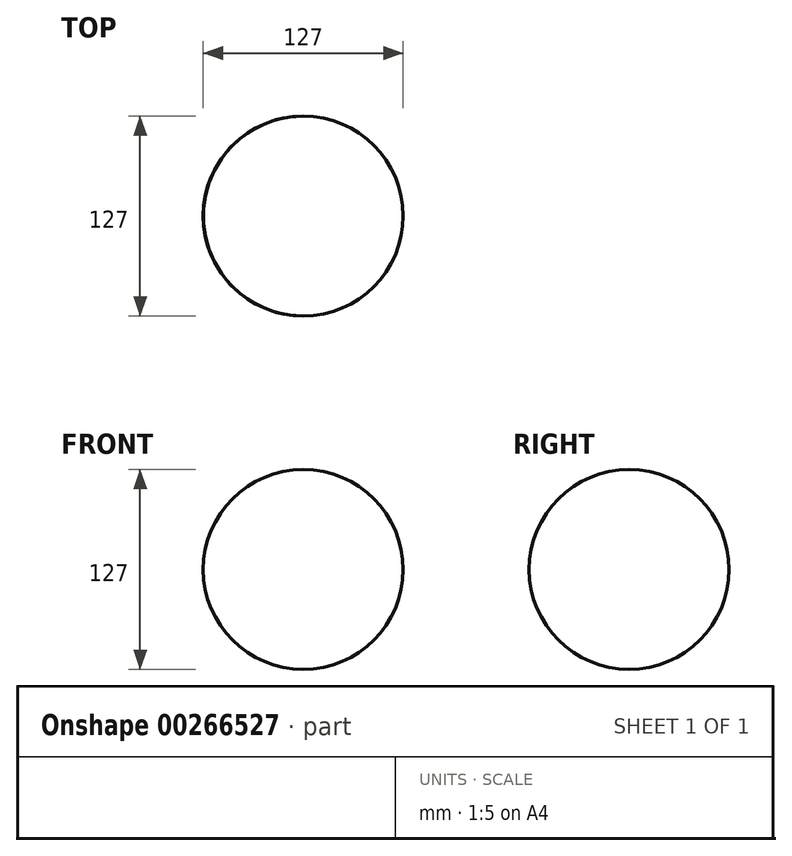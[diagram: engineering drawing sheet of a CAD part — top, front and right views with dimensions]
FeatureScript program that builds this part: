
annotation { "Feature Type Name" : "Feature", "Feature Type Description" : "" }
export const myFeature = defineFeature(function(context is Context, id is Id, definition is map)
    precondition{}
    {
        {
            var Q0;
            Q0=qCreatedBy(makeId("Top.planeOp"),FACE);
            var sketch = newSketch(context, id + "F0", { "sketchPlane" : qUnion([Q0])});
            skLineSegment(sketch, "E0.bottom", {"start": v(-63.5, 63.5) * mm, "end": v(0, 63.5) * mm});
            skLineSegment(sketch, "E0.top", {"start": v(-63.5, -63.5) * mm, "end": v(0, -63.5) * mm});
            skLineSegment(sketch, "E0.left", {"start": v(-63.5, 63.5) * mm, "end": v(-63.5, -63.5) * mm});
            skLineSegment(sketch, "E0.right", {"start": v(0, 63.5) * mm, "end": v(0, -63.5) * mm});
            skSolve(sketch);
        }
        {
            var Q0;
            Q0=makeQuery(id+"F0.imprint","IMPRINT",FACE,{"disambiguationData":[TD([[makeQuery(id+"F0.imprint","IMPRINT",EDGE,{"derivedFrom":sQuery(id+"F0.wireOp",EDGE,"E0.bottom")}),-1.0]])]});
            var Q1;
            Q1=sQuery(id+"F0.wireOp",EDGE,"E0.right");
            revolve(context, id + "F1", {"entities" : qUnion([Q0]), "axis" : qUnion([Q1]), "revolveType" : RevolveType.FULL});
        }
        {
            var Q0;
            Q0=qCreatedBy(makeId("Top.planeOp"),FACE);
            var sketch = newSketch(context, id + "F2", { "sketchPlane" : qUnion([Q0])});
            skArc(sketch, "E1", {"start": v(0, 63.5) * mm, "mid": v(63.5, 0) * mm, "end": v(0, -63.5) * mm});
            skLineSegment(sketch, "E2", {"start": v(0, -63.5) * mm, "end": v(0, 63.5) * mm});
            skSolve(sketch);
        }
        {
            var Q0;
            Q0 = qSketchRegion(id + "F2", true);
            var Q1;
            Q1=sQuery(id+"F2.wireOp",EDGE,"E1");
            var Q2;
            Q2=sQuery(id+"F2.wireOp",EDGE,"E2");
            var Q3;
            Q3=sQuery(id+"F2.wireOp",EDGE,"E2");
            revolve(context, id + "F3", {"operationType" : NewBodyOperationType.INTERSECT, "entities" : qUnion([Q0]), "surfaceEntities" : qUnion([Q1, Q2]), "axis" : qUnion([Q3]), "revolveType" : RevolveType.FULL, "oppositeDirection" : true});
        }
    });
